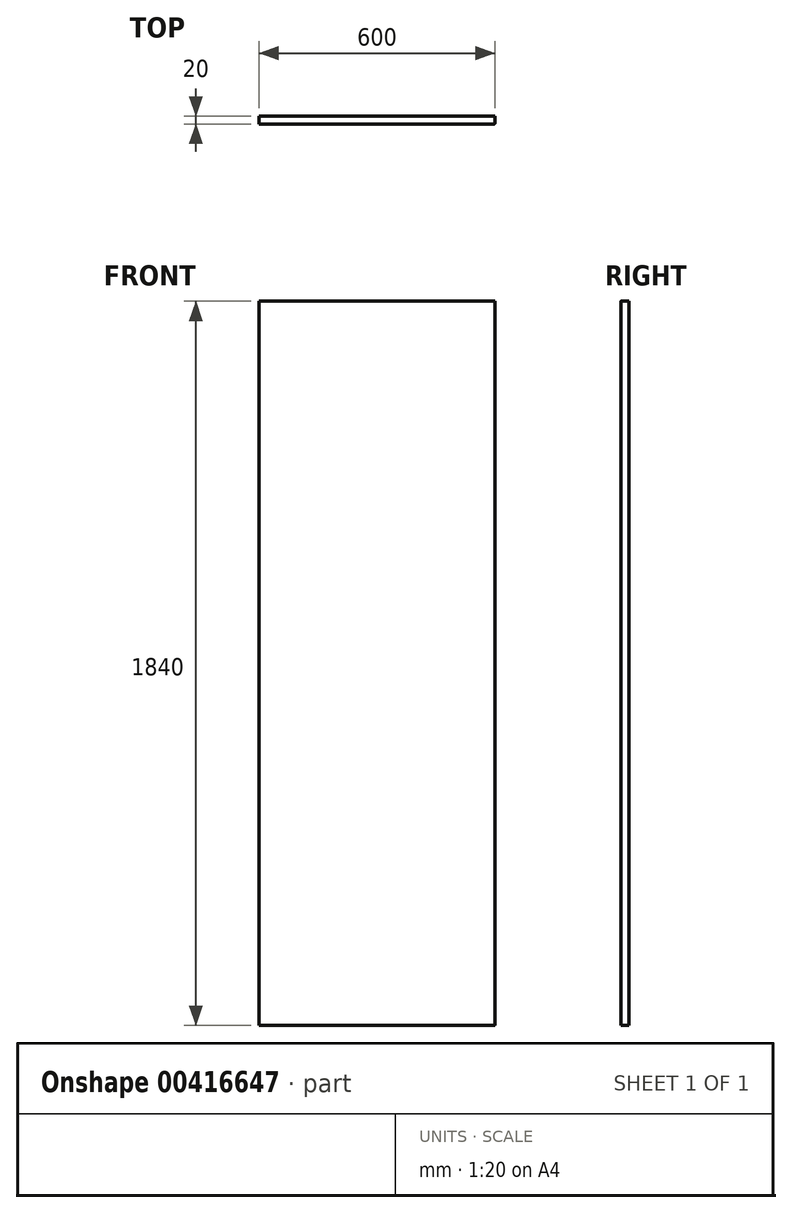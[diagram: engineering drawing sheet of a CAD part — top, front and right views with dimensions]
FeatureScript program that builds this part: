
annotation { "Feature Type Name" : "Feature", "Feature Type Description" : "" }
export const myFeature = defineFeature(function(context is Context, id is Id, definition is map)
    precondition{}
    {
        {
            var Q0;
            Q0=qCreatedBy(makeId("Front.planeOp"),FACE);
            var sketch = newSketch(context, id + "F0", { "sketchPlane" : qUnion([Q0])});
            skLineSegment(sketch, "E0", {"start": v(0, -4.48) * mm, "end": v(0, 1835.52) * mm});
            skLineSegment(sketch, "E1", {"start": v(0, 1835.52) * mm, "end": v(600, 1835.52) * mm});
            skLineSegment(sketch, "E2", {"start": v(0, -4.48) * mm, "end": v(600, -4.48) * mm});
            skLineSegment(sketch, "E3", {"start": v(600, 1835.52) * mm, "end": v(600, -4.48) * mm});
            skSolve(sketch);
        }
        {
            var Q0;
            Q0=qSketchRegion(id+"F0",true);
            var Q1;
            Q1=makeQuery(id+"F0.imprint","IMPRINT",FACE,{"disambiguationData":[TD([[makeQuery(id+"F0.imprint","IMPRINT",EDGE,{"derivedFrom":sQuery(id+"F0.wireOp",EDGE,"E0")}),-1.0]])]});
            extrude(context, id + "F1", {"entities" : qUnion([Q0, Q1]), "depth" : 20 * mm});
        }
        {
            var Q0;
            Q0=makeQuery(id+"F1.opExtrude","CAP_EDGE",EDGE,{"disambiguationData":[OSD([sQuery(id+"F0.wireOp",EDGE,"E3")])],"isStart":false});
            fillet(context, id + "F2", {"entities" : qUnion([Q0]), "radius" : 2 * mm, "tangentPropagation" : true, "allowEdgeOverflow" : false});
        }
    });
